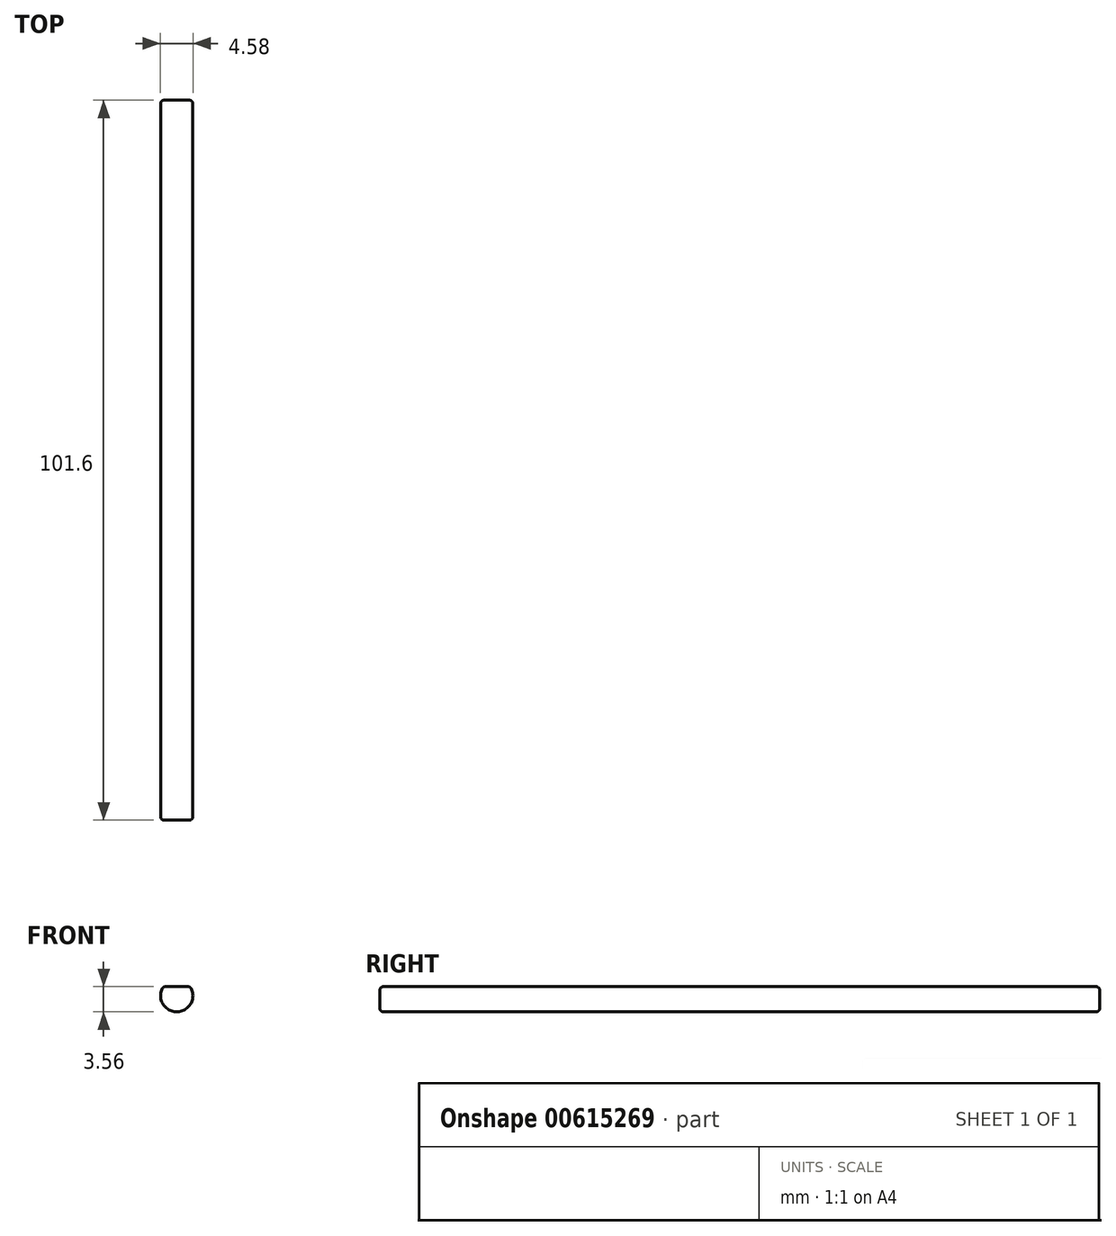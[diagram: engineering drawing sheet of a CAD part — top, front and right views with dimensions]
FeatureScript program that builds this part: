
annotation { "Feature Type Name" : "Feature", "Feature Type Description" : "" }
export const myFeature = defineFeature(function(context is Context, id is Id, definition is map)
    precondition{}
    {
        {
            var Q0;
            Q0=qCreatedBy(makeId("Front.planeOp"),FACE);
            var sketch = newSketch(context, id + "F0", { "sketchPlane" : qUnion([Q0])});
            skCircle(sketch, "E0", {"center": v(0, 0) * mm, "radius": 2.29 * mm});
            skLineSegment(sketch, "E1", {"start": v(-1.9, 1.27) * mm, "end": v(1.9, 1.27) * mm});
            skPoint(sketch, "E2", {"position": v(0, 2.29) * mm});
            skSolve(sketch);
        }
        {
            var Q0;
            {var subQ0=sQuery(id+"F0.wireOp",EDGE,"E1");Q0=makeQuery(id+"F0.imprint","IMPRINT",FACE,{"disambiguationData":[TD([[makeQuery(id+"F0.imprint","IMPRINT",EDGE,{"derivedFrom":subQ0}),-1.0]])]});}
            extrude(context, id + "F1", {"entities" : qUnion([Q0]), "depth" : 101.6 * mm, "offsetDistance" : 25.4 * mm});
        }
        {
            var Q0;
            {var subQ0=sQuery(id+"F0.wireOp",EDGE,"E1");var subQ1=sQuery(id+"F0.wireOp",EDGE,"E0");Q0=makeQuery(id+"F1.opExtrude","SWEPT_EDGE",EDGE,{"disambiguationData":[OSD([subQ1,subQ0]),TDD([makeQuery(id+"F0.imprint","INTERSECT",VERTEX,{"disambiguationData":[OD(0.0)],"derivedFrom":[subQ1,subQ0]})])]});}
            var Q1;
            {var subQ0=sQuery(id+"F0.wireOp",EDGE,"E1");var subQ1=sQuery(id+"F0.wireOp",EDGE,"E0");Q1=makeQuery(id+"F1.opExtrude","SWEPT_EDGE",EDGE,{"disambiguationData":[OSD([subQ1,subQ0]),TDD([makeQuery(id+"F0.imprint","INTERSECT",VERTEX,{"disambiguationData":[OD(1.0)],"derivedFrom":[subQ1,subQ0]})])]});}
            var Q2;
            Q2=makeQuery(id+"F1.opExtrude","CAP_EDGE",EDGE,{"disambiguationData":[OSD([sQuery(id+"F0.wireOp",EDGE,"E1")])],"isStart":false});
            var Q3;
            Q3=makeQuery(id+"F1.opExtrude","CAP_EDGE",EDGE,{"disambiguationData":[OSD([sQuery(id+"F0.wireOp",EDGE,"E0")])],"isStart":false});
            var Q4;
            Q4=makeQuery(id+"F1.opExtrude","CAP_EDGE",EDGE,{"disambiguationData":[OSD([sQuery(id+"F0.wireOp",EDGE,"E1")])],"isStart":true});
            var Q5;
            Q5=makeQuery(id+"F1.opExtrude","CAP_EDGE",EDGE,{"disambiguationData":[OSD([sQuery(id+"F0.wireOp",EDGE,"E0")])],"isStart":true});
            fillet(context, id + "F2", {"entities" : qUnion([Q0, Q1, Q2, Q3, Q4, Q5]), "radius" : 0.5 * mm, "tangentPropagation" : true, "allowEdgeOverflow" : false});
        }
    });
